# Revit family: Hager-VOLTA-Flush_mounted-Other-Without_Cover-Without_DIN-Hosted-DE-de
name_source: partatom
category: Electrical Equipment
units: mm (PartAtom-declared; Revit-internal decimal feet)

## family parameters
Cut with Voids When Loaded = No
Host = Face
Maintain Annotation Orientation = Yes
Panel Configuration = Two Columns, Circuits Across
Part Type = Panelboard
Room Calculation Point = No
Round Connector Dimension = Use Diameter
Shared = No

## types (5) — shared parameters
BC_MODEL_ID = 1547171
BC_OBJECT_ID = 513477
BC_OBJECT_VERSION = #3
Code hager = ADD-EC000214_EU
EF000003 - Montageart = Unterputz
EF000024 - UV-beständig = No
EF000118 - Mit Montageplatte = No
EF000218 - Einbautiefe = 90 mm  [stored 0.295276 ft]
EF000846 - Einbaubreite = 314 mm  [stored 1.03018 ft]
EF001088 - Anbaumöglichkeit = Yes
EF001134 - DIN-Schiene = No
EF002950 - Breite in Teilungseinheiten = 12
EF005474 - Schutzart (IP) = sonstige
EF006244 - Transparenter Deckel/Tür = No
EF006306 - Mit Schloss = No
EF015776 - Erdungsklemmenblock = No
EF015777 - Neutralleiterklemmenblock = No
EF015941 - Signaldurchlassende Tür = No
ETIM class code = EC000214
ETIM class name = Small distribution board
HG000002-Mit tür = No
HG000003-Bereich = VOLTA
HG000005-Dicke = 2 mm  [stored 0.00656168 ft]
HG000006-Flush mounted = Yes
HG000009-Doppelflügeligen Tür = No
HG000010-Asymmetrische Türen = No
HG000011-Leere Reihen von unten = No
HG000012-Türschwenkwinkel = 90.00°
HG000013-Tür links = No
HG000014-Tür rechts = Yes
HG000015-Sichtbarkeit der Türöffnung = Yes
HG000016-3D-Türsichtbarkeit = Yes
HG000017-Distanz zwischen den Polen = 18 mm  [stored 0.0590551 ft]
HG000099-Onfly Template ID-de-DE = 507532
HGEF0002950-Breite in Teilungseinheiten = 12
Manufacturer = Hager
Name = VOLTA-Flush_mounted-Other-Without_Cover-Without_DIN-DE
Name BIM&CO = Electricity
Name hager = ADD_Enclosures_EC000214
Uniformat = Low Tension Service & Dist.
Uniformat code = D501001
zero-valued in all types: Default Elevation, EF001131 - Innentiefe, HG000001-Anzahl der Spalten, HG000007-Anzahl der leeren Spalten, HG000008-Anzahl der leeren Reihen

## per-type parameters (varying)
| type | BC_VARIANT_ID | EF000007 - Farbe | EF000008 - Breite | EF000040 - Höhe | EF000049 - Tiefe | EF000116 - RAL-Nummer | EF000266 - Anzahl der Reihen | EF000332 - Einbauhöhe | EF001062 - EMV-Ausführung | EF004462 - Art der Schließung | EF009212 - Ausführung Deckel | HG000004-Herstellerreferenz | HG000060-RAL-number | HGEF000266-Anzahl der Reihen |
| VOLTA-Flush_mounted_W330_H355_D94_12_Modular_Spacing-VU12NK | 1174205 | grau | 330 mm | 355 mm | 94 mm  [stored 0.308399 ft] | 7035 | 1 | 346 mm  [stored 1.13517 ft] | Yes |  | geschlossen | VU12NK | 7035 | 1 |
| VOLTA-Flush_mounted_W348_H505_D98_12_Modular_Spacing-VU24NK | 1174206 | weiß | 348 mm  [stored 1.14173 ft] | 505 mm  [stored 1.65682 ft] | 98 mm  [stored 0.321522 ft] | 9010 | 2 | 471 mm  [stored 1.54528 ft] | No | sonstige |  | VU24NK | 9010 | 2 |
| VOLTA-Flush_mounted_W348_H630_D98_12_Modular_Spacing-VU36NK | 1174208 | weiß | 348 mm  [stored 1.14173 ft] | 630 mm  [stored 2.06693 ft] | 98 mm  [stored 0.321522 ft] | 9010 | 3 | 596 mm  [stored 1.95538 ft] | No | sonstige |  | VU36NK | 9010 | 3 |
| VOLTA-Flush_mounted_W348_H755_D98_12_Modular_Spacing-VU48NK | 1174209 | weiß | 348 mm  [stored 1.14173 ft] | 755 mm  [stored 2.47703 ft] | 98 mm  [stored 0.321522 ft] | 9010 | 4 | 721 mm  [stored 2.36549 ft] | No | sonstige |  | VU48NK | 9010 | 4 |
| VOLTA-Flush_mounted_W348_H880_D98_12_Modular_Spacing-VU60NK | 1174210 | weiß | 348 mm  [stored 1.14173 ft] | 880 mm  [stored 2.88714 ft] | 98 mm  [stored 0.321522 ft] | 9010 | 5 | 865 mm  [stored 2.83793 ft] | No | sonstige |  | VU60NK | 9010 | 5 |

note: column(s) folded — value = type name in every type: Reference

note: [stored X ft] marks values corroborated as IEEE doubles in the binary element streams (Revit-internal decimal feet)

## geometry (parser evidence)
native form markers: Sweep x14
no freeform markers — native parametric forms only
